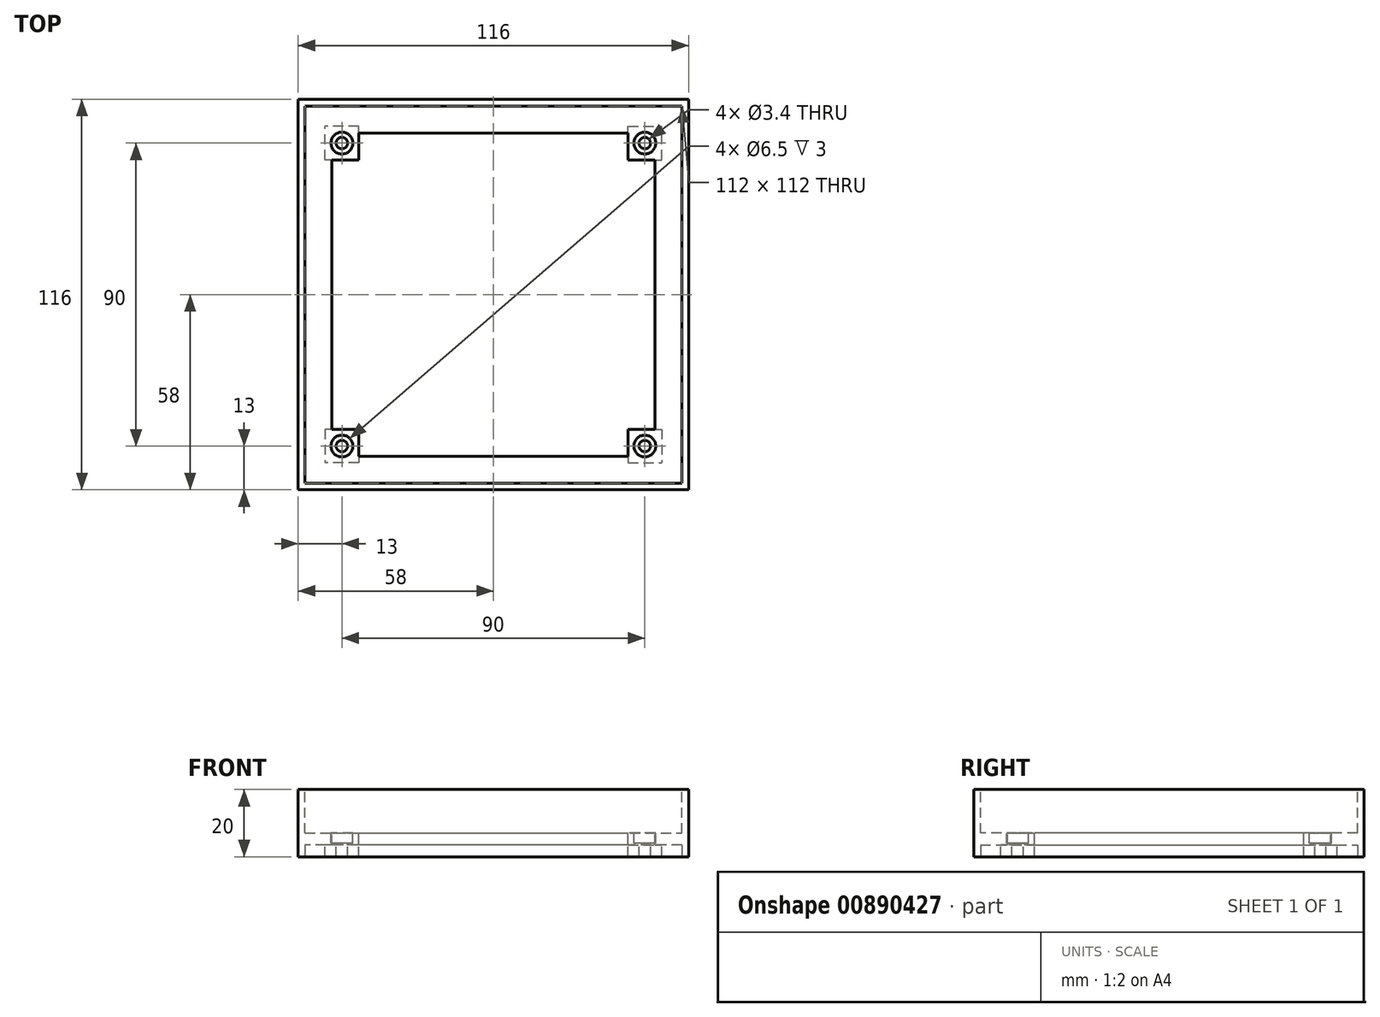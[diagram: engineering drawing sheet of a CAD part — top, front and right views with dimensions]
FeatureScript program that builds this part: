
annotation { "Feature Type Name" : "Feature", "Feature Type Description" : "" }
export const myFeature = defineFeature(function(context is Context, id is Id, definition is map)
    precondition{}
    {
        {
            var Q0;
            Q0=qCreatedBy(makeId("Top.planeOp"),FACE);
            var sketch = newSketch(context, id + "F0", { "sketchPlane" : qUnion([Q0])});
            skLineSegment(sketch, "E0.bottom", {"start": v(58, -58) * mm, "end": v(-58, -58) * mm});
            skLineSegment(sketch, "E0.top", {"start": v(58, 58) * mm, "end": v(-58, 58) * mm});
            skLineSegment(sketch, "E0.left", {"start": v(58, -58) * mm, "end": v(58, 58) * mm});
            skLineSegment(sketch, "E0.right", {"start": v(-58, -58) * mm, "end": v(-58, 58) * mm});
            skPoint(sketch, "E0.middle", {"position": v(0, 0) * mm});
            skSolve(sketch);
        }
        {
            var Q0;
            Q0 = qSketchRegion(id + "F0", true);
            extrude(context, id + "F1", {"entities" : qUnion([Q0]), "depth" : 20 * mm, "offsetDistance" : 25 * mm});
        }
        {
            var Q0;
            Q0=makeQuery(id+"F1.opExtrude","CAP_FACE",FACE,{"disambiguationData":[OSD([sQuery(id+"F0.wireOp",EDGE,"E0.bottom"),sQuery(id+"F0.wireOp",EDGE,"E0.top"),sQuery(id+"F0.wireOp",EDGE,"E0.left"),sQuery(id+"F0.wireOp",EDGE,"E0.right")])],"isStart":false});
            var sketch = newSketch(context, id + "F2", { "sketchPlane" : qUnion([Q0])});
            skLineSegment(sketch, "E1.bottom", {"start": v(-58, 58) * mm, "end": v(58, 58) * mm});
            skLineSegment(sketch, "E1.top", {"start": v(-58, -58) * mm, "end": v(58, -58) * mm});
            skLineSegment(sketch, "E1.left", {"start": v(-58, 58) * mm, "end": v(-58, -58) * mm});
            skLineSegment(sketch, "E1.right", {"start": v(58, 58) * mm, "end": v(58, -58) * mm});
            skPoint(sketch, "E1.middle", {"position": v(0, 0) * mm});
            skLineSegment(sketch, "E2.0", {"start": v(-56, 56) * mm, "end": v(56, 56) * mm});
            skLineSegment(sketch, "E2.1", {"start": v(-56, 56) * mm, "end": v(-56, -56) * mm});
            skLineSegment(sketch, "E2.2", {"start": v(-56, -56) * mm, "end": v(56, -56) * mm});
            skLineSegment(sketch, "E2.3", {"start": v(56, 56) * mm, "end": v(56, -56) * mm});
            skSolve(sketch);
        }
        {
            var Q0;
            Q0=makeQuery(id+"F2.imprint","IMPRINT",FACE,{"disambiguationData":[TD([[makeQuery(id+"F2.imprint","IMPRINT",EDGE,{"derivedFrom":sQuery(id+"F2.wireOp",EDGE,"E2.0")}),-1.0]])]});
            extrude(context, id + "F3", {"entities" : qUnion([Q0]), "operationType" : NewBodyOperationType.REMOVE, "oppositeDirection" : true, "depth" : 13 * mm, "offsetDistance" : 25 * mm});
        }
        {
            var Q0;
            Q0=makeQuery(id+"F3.boolean.opBoolean","COPY",FACE,{"derivedFrom":makeQuery(id+"F3.opExtrude","CAP_FACE",FACE,{"disambiguationData":[OSD([sQuery(id+"F2.wireOp",EDGE,"E2.0"),sQuery(id+"F2.wireOp",EDGE,"E2.1"),sQuery(id+"F2.wireOp",EDGE,"E2.2"),sQuery(id+"F2.wireOp",EDGE,"E2.3")])],"isStart":false})});
            var sketch = newSketch(context, id + "F4", { "sketchPlane" : qUnion([Q0])});
            skLineSegment(sketch, "E3.0", {"start": v(48, -48) * mm, "end": v(48, 48) * mm});
            skLineSegment(sketch, "E3.1", {"start": v(-48, -48) * mm, "end": v(48, -48) * mm});
            skLineSegment(sketch, "E3.2", {"start": v(-48, 48) * mm, "end": v(-48, -48) * mm});
            skLineSegment(sketch, "E3.3", {"start": v(48, 48) * mm, "end": v(-48, 48) * mm});
            skSolve(sketch);
        }
        {
            var Q0;
            Q0=makeQuery(id+"F4.imprint","IMPRINT",FACE,{"disambiguationData":[TD([[makeQuery(id+"F4.imprint","IMPRINT",EDGE,{"derivedFrom":sQuery(id+"F4.wireOp",EDGE,"E3.0")}),1.0]])]});
            var Q1;
            Q1=makeQuery(id+"F1.opExtrude","CAP_FACE",FACE,{"disambiguationData":[OSD([sQuery(id+"F0.wireOp",EDGE,"E0.bottom"),sQuery(id+"F0.wireOp",EDGE,"E0.top"),sQuery(id+"F0.wireOp",EDGE,"E0.left"),sQuery(id+"F0.wireOp",EDGE,"E0.right")])],"isStart":true});
            extrude(context, id + "F5", {"entities" : qUnion([Q0]), "operationType" : NewBodyOperationType.REMOVE, "endBound" : BoundingType.UP_TO_SURFACE, "oppositeDirection" : true, "depth" : 25 * mm, "endBoundEntityFace" : qUnion([Q1]), "offsetDistance" : 25 * mm});
        }
        {
            var Q0;
            Q0=makeQuery(id+"F1.opExtrude","CAP_FACE",FACE,{"disambiguationData":[OSD([sQuery(id+"F0.wireOp",EDGE,"E0.bottom"),sQuery(id+"F0.wireOp",EDGE,"E0.top"),sQuery(id+"F0.wireOp",EDGE,"E0.left"),sQuery(id+"F0.wireOp",EDGE,"E0.right")])],"isStart":true});
            var sketch = newSketch(context, id + "F6", { "sketchPlane" : qUnion([Q0])});
            skLineSegment(sketch, "E4.0", {"start": v(56, 56) * mm, "end": v(-56, 56) * mm});
            skLineSegment(sketch, "E4.1", {"start": v(56, 56) * mm, "end": v(56, -56) * mm});
            skLineSegment(sketch, "E4.2", {"start": v(56, -56) * mm, "end": v(-56, -56) * mm});
            skLineSegment(sketch, "E4.3", {"start": v(-56, 56) * mm, "end": v(-56, -56) * mm});
            skSolve(sketch);
        }
        {
            var Q0;
            Q0=makeQuery(id+"F6.imprint","IMPRINT",FACE,{"disambiguationData":[TD([[makeQuery(id+"F6.imprint","IMPRINT",EDGE,{"derivedFrom":sQuery(id+"F6.wireOp",EDGE,"E4.0")}),1.0]])]});
            extrude(context, id + "F7", {"entities" : qUnion([Q0]), "operationType" : NewBodyOperationType.REMOVE, "oppositeDirection" : true, "depth" : 3.5 * mm, "offsetDistance" : 25 * mm});
        }
        {
            var Q0;
            Q0=makeQuery(id+"F3.boolean.opBoolean","COPY",FACE,{"derivedFrom":makeQuery(id+"F3.opExtrude","CAP_FACE",FACE,{"disambiguationData":[OSD([sQuery(id+"F2.wireOp",EDGE,"E2.0"),sQuery(id+"F2.wireOp",EDGE,"E2.1"),sQuery(id+"F2.wireOp",EDGE,"E2.2"),sQuery(id+"F2.wireOp",EDGE,"E2.3")])],"isStart":false})});
            var sketch = newSketch(context, id + "F8", { "sketchPlane" : qUnion([Q0])});
            skLineSegment(sketch, "E5.bottom", {"start": v(-50, 50) * mm, "end": v(-40, 50) * mm});
            skLineSegment(sketch, "E5.top", {"start": v(-50, 40) * mm, "end": v(-40, 40) * mm});
            skLineSegment(sketch, "E5.left", {"start": v(-50, 50) * mm, "end": v(-50, 40) * mm});
            skLineSegment(sketch, "E5.right", {"start": v(-40, 50) * mm, "end": v(-40, 40) * mm});
            skLineSegment(sketch, "E6.bottom", {"start": v(50, 50) * mm, "end": v(40, 50) * mm});
            skLineSegment(sketch, "E6.top", {"start": v(50, 40) * mm, "end": v(40, 40) * mm});
            skLineSegment(sketch, "E6.left", {"start": v(50, 50) * mm, "end": v(50, 40) * mm});
            skLineSegment(sketch, "E6.right", {"start": v(40, 50) * mm, "end": v(40, 40) * mm});
            skLineSegment(sketch, "E7.bottom", {"start": v(-50, -50) * mm, "end": v(-40, -50) * mm});
            skLineSegment(sketch, "E7.top", {"start": v(-50, -40) * mm, "end": v(-40, -40) * mm});
            skLineSegment(sketch, "E7.left", {"start": v(-50, -50) * mm, "end": v(-50, -40) * mm});
            skLineSegment(sketch, "E7.right", {"start": v(-40, -50) * mm, "end": v(-40, -40) * mm});
            skLineSegment(sketch, "E8.bottom", {"start": v(50, -50) * mm, "end": v(40, -50) * mm});
            skLineSegment(sketch, "E8.top", {"start": v(50, -40) * mm, "end": v(40, -40) * mm});
            skLineSegment(sketch, "E8.left", {"start": v(50, -50) * mm, "end": v(50, -40) * mm});
            skLineSegment(sketch, "E8.right", {"start": v(40, -50) * mm, "end": v(40, -40) * mm});
            skSolve(sketch);
        }
        {
            var Q0;
            Q0 = qSketchRegion(id + "F8", true);
            var Q1;
            Q1=makeQuery(id+"F1.opExtrude","CAP_FACE",FACE,{"disambiguationData":[OSD([sQuery(id+"F0.wireOp",EDGE,"E0.bottom"),sQuery(id+"F0.wireOp",EDGE,"E0.top"),sQuery(id+"F0.wireOp",EDGE,"E0.left"),sQuery(id+"F0.wireOp",EDGE,"E0.right")])],"isStart":true});
            extrude(context, id + "F9", {"entities" : qUnion([Q0]), "operationType" : NewBodyOperationType.ADD, "endBound" : BoundingType.UP_TO_SURFACE, "oppositeDirection" : true, "depth" : 25 * mm, "endBoundEntityFace" : qUnion([Q1]), "offsetDistance" : 25 * mm});
        }
        {
            var Q0;
            Q0=makeQuery(id+"F9.boolean.opBoolean","MERGE",FACE,{"derivedFrom":[makeQuery(id+"F3.boolean.opBoolean","COPY",FACE,{"derivedFrom":makeQuery(id+"F3.opExtrude","CAP_FACE",FACE,{"disambiguationData":[OSD([sQuery(id+"F2.wireOp",EDGE,"E2.0"),sQuery(id+"F2.wireOp",EDGE,"E2.1"),sQuery(id+"F2.wireOp",EDGE,"E2.2"),sQuery(id+"F2.wireOp",EDGE,"E2.3")])],"isStart":false})}),makeQuery(id+"F9.opExtrude","CAP_FACE",FACE,{"disambiguationData":[OSD([sQuery(id+"F8.wireOp",EDGE,"vYML6lXM-SVMj-JF0E-N7rK-HPYk551oT2rf.bottom"),sQuery(id+"F8.wireOp",EDGE,"vYML6lXM-SVMj-JF0E-N7rK-HPYk551oT2rf.top"),sQuery(id+"F8.wireOp",EDGE,"vYML6lXM-SVMj-JF0E-N7rK-HPYk551oT2rf.left"),sQuery(id+"F8.wireOp",EDGE,"vYML6lXM-SVMj-JF0E-N7rK-HPYk551oT2rf.right")])],"isStart":true}),makeQuery(id+"F9.opExtrude","CAP_FACE",FACE,{"disambiguationData":[OSD([sQuery(id+"F8.wireOp",EDGE,"WHYMQ1Q8-A5kD-iplV-UY9v-NRmDNsHMkbVs.bottom"),sQuery(id+"F8.wireOp",EDGE,"WHYMQ1Q8-A5kD-iplV-UY9v-NRmDNsHMkbVs.top"),sQuery(id+"F8.wireOp",EDGE,"WHYMQ1Q8-A5kD-iplV-UY9v-NRmDNsHMkbVs.left"),sQuery(id+"F8.wireOp",EDGE,"WHYMQ1Q8-A5kD-iplV-UY9v-NRmDNsHMkbVs.right")])],"isStart":true}),makeQuery(id+"F9.opExtrude","CAP_FACE",FACE,{"disambiguationData":[OSD([sQuery(id+"F8.wireOp",EDGE,"mnqmVZLQ-4gVp-IMSz-V2s2-aDw2SOQePGdS.bottom"),sQuery(id+"F8.wireOp",EDGE,"mnqmVZLQ-4gVp-IMSz-V2s2-aDw2SOQePGdS.top"),sQuery(id+"F8.wireOp",EDGE,"mnqmVZLQ-4gVp-IMSz-V2s2-aDw2SOQePGdS.left"),sQuery(id+"F8.wireOp",EDGE,"mnqmVZLQ-4gVp-IMSz-V2s2-aDw2SOQePGdS.right")])],"isStart":true}),makeQuery(id+"F9.opExtrude","CAP_FACE",FACE,{"disambiguationData":[OSD([sQuery(id+"F8.wireOp",EDGE,"O7LesDHs-mNha-iT3F-jr9l-qWC4LM4io0Ih.bottom"),sQuery(id+"F8.wireOp",EDGE,"O7LesDHs-mNha-iT3F-jr9l-qWC4LM4io0Ih.top"),sQuery(id+"F8.wireOp",EDGE,"O7LesDHs-mNha-iT3F-jr9l-qWC4LM4io0Ih.left"),sQuery(id+"F8.wireOp",EDGE,"O7LesDHs-mNha-iT3F-jr9l-qWC4LM4io0Ih.right")])],"isStart":true})]});
            var sketch = newSketch(context, id + "F10", { "sketchPlane" : qUnion([Q0])});
            skLineSegment(sketch, "E9.bottom", {"start": v(-40, 40) * mm, "end": v(-50, 40) * mm, "construction": true});
            skLineSegment(sketch, "E9.top", {"start": v(-40, 50) * mm, "end": v(-50, 50) * mm, "construction": true});
            skLineSegment(sketch, "E9.left", {"start": v(-40, 40) * mm, "end": v(-40, 50) * mm, "construction": true});
            skLineSegment(sketch, "E9.right", {"start": v(-50, 40) * mm, "end": v(-50, 50) * mm, "construction": true});
            skPoint(sketch, "E10", {"position": v(-45, 45) * mm});
            skPoint(sketch, "E10.positionSnap0", {"position": v(-50, 45) * mm});
            skPoint(sketch, "E10.positionSnap1", {"position": v(-45, 50) * mm});
            skLineSegment(sketch, "E11.bottom", {"start": v(40, 40) * mm, "end": v(50, 40) * mm, "construction": true});
            skLineSegment(sketch, "E11.top", {"start": v(40, 50) * mm, "end": v(50, 50) * mm, "construction": true});
            skLineSegment(sketch, "E11.left", {"start": v(40, 40) * mm, "end": v(40, 50) * mm, "construction": true});
            skLineSegment(sketch, "E11.right", {"start": v(50, 40) * mm, "end": v(50, 50) * mm, "construction": true});
            skLineSegment(sketch, "E12.bottom", {"start": v(-40, -40) * mm, "end": v(-50, -40) * mm, "construction": true});
            skLineSegment(sketch, "E12.top", {"start": v(-40, -50) * mm, "end": v(-50, -50) * mm, "construction": true});
            skLineSegment(sketch, "E12.left", {"start": v(-40, -40) * mm, "end": v(-40, -50) * mm, "construction": true});
            skLineSegment(sketch, "E12.right", {"start": v(-50, -40) * mm, "end": v(-50, -50) * mm, "construction": true});
            skLineSegment(sketch, "E13.bottom", {"start": v(40, -40) * mm, "end": v(50, -40) * mm, "construction": true});
            skLineSegment(sketch, "E13.top", {"start": v(40, -50) * mm, "end": v(50, -50) * mm, "construction": true});
            skLineSegment(sketch, "E13.left", {"start": v(40, -40) * mm, "end": v(40, -50) * mm, "construction": true});
            skLineSegment(sketch, "E13.right", {"start": v(50, -40) * mm, "end": v(50, -50) * mm, "construction": true});
            skPoint(sketch, "E14", {"position": v(-45, -45) * mm});
            skPoint(sketch, "E14.positionSnap0", {"position": v(-45, -50) * mm});
            skPoint(sketch, "E14.positionSnap1", {"position": v(-50, -45) * mm});
            skPoint(sketch, "E15", {"position": v(45, -45) * mm});
            skPoint(sketch, "E15.positionSnap0", {"position": v(45, -50) * mm});
            skPoint(sketch, "E15.positionSnap1", {"position": v(50, -45) * mm});
            skPoint(sketch, "E16", {"position": v(45, 45) * mm});
            skPoint(sketch, "E16.positionSnap0", {"position": v(50, 45) * mm});
            skPoint(sketch, "E16.positionSnap1", {"position": v(45, 50) * mm});
            skSolve(sketch);
        }
        {
            var Q0;
            Q0=sQuery(id+"F10.wireOp",VERTEX,"E16");
            var Q1;
            Q1=sQuery(id+"F10.wireOp",VERTEX,"E10");
            var Q2;
            Q2=sQuery(id+"F10.wireOp",VERTEX,"E14");
            var Q3;
            Q3=sQuery(id+"F10.wireOp",VERTEX,"E15");
            var Q4;
            Q4=makeQuery(id+"F1.opExtrude","SWEPT_BODY",BODY,{"disambiguationData":[OSD([sQuery(id+"F0.wireOp",EDGE,"E0.bottom"),sQuery(id+"F0.wireOp",EDGE,"E0.top"),sQuery(id+"F0.wireOp",EDGE,"E0.left"),sQuery(id+"F0.wireOp",EDGE,"E0.right")])]});
            hole(context, id + "F11", {"style" : HoleStyle.C_BORE, "endStyle" : HoleEndStyle.THROUGH, "standardTappedOrClearance" : lookupTablePath({ "fit" : "Normal", "standard" : "ISO", "size" : "M3", "type" : "Clearance" }), "standardBlindInLast" : lookupTablePath({ "fit" : "Normal", "standard" : "ISO", "size" : "M3", "type" : "Clearance" }), "holeDiameter" : 3.4 * mm, "cBoreDiameter" : 6.5 * mm, "cBoreDepth" : 3 * mm, "majorDiameter" : 3 * mm, "isTappedThrough" : true, "tappedDepth" : 12 * mm, "tapClearance" : 3, "locations" : qUnion([Q0, Q1, Q2, Q3]), "scope" : qUnion([Q4])});
        }
    });
